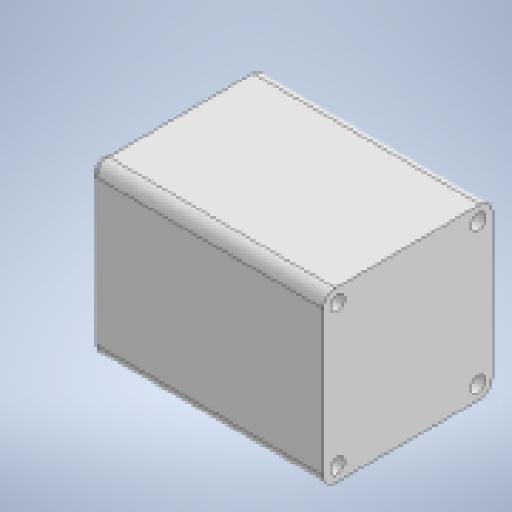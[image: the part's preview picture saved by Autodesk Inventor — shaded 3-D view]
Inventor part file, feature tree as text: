
AUTODESK INVENTOR PART (.ipt)
format: ipt  version: 2023 (Build 270158000, 158)  size: 156,160 bytes
history: native  units: mm
features: extrude x3, sketch x3
ambient origin geometry x8: Origin, YZ Plane, XZ Plane, XY Plane, X Axis, Y Axis, Z Axis, Center Point
bodies: Solid1 (feature_tree)
feature tree (6):
  extrude  "Extrusion1"  Depth=56.4mm
  extrude  "Extrusion2"  Depth=4.0mm
  extrude  "Extrusion3"  Depth=4.0mm
  sketch  "Sketch1"  dims[d0=56.4mm d1=47.14mm]
  sketch  "Sketch2"  dims[d2=5.0mm d3=4.0mm]
  sketch  "Sketch3"  dims[d4=4.0mm d5=4.0mm d6=4.0mm d7=76.0mm d8=0.0mm d9=38.1mm d10=1.6mm d11=0.0mm d12=6.35mm d13=24.0mm d14=0.0mm]
